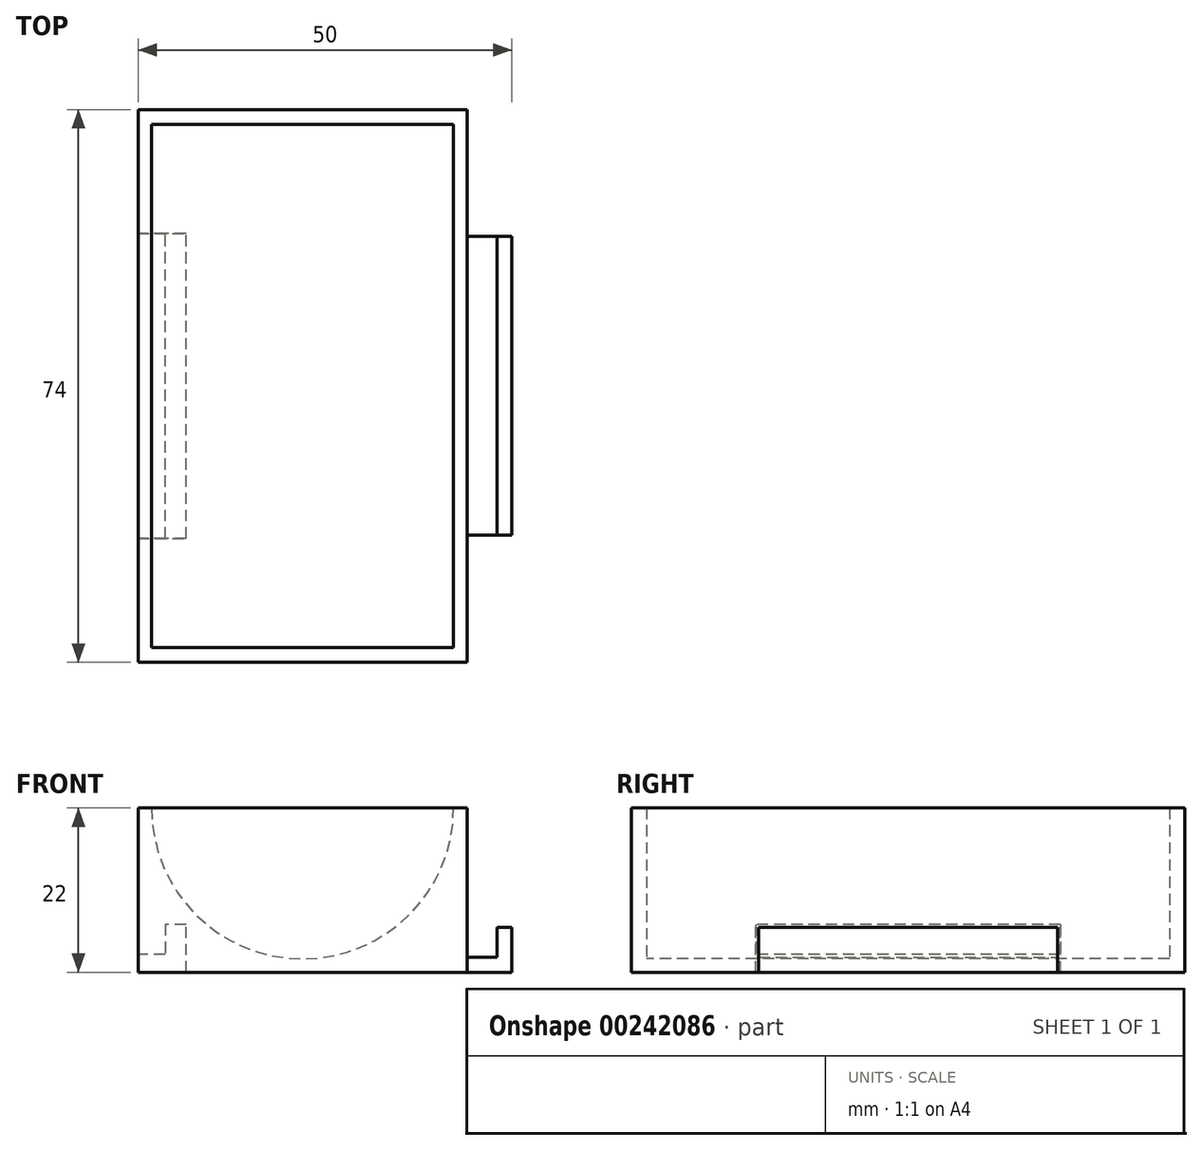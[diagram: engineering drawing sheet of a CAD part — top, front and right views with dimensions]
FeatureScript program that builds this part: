
annotation { "Feature Type Name" : "Feature", "Feature Type Description" : "" }
export const myFeature = defineFeature(function(context is Context, id is Id, definition is map)
    precondition{}
    {
        {
            var Q0;
            Q0=qCreatedBy(makeId("Top.planeOp"),FACE);
            var sketch = newSketch(context, id + "F0", { "sketchPlane" : qUnion([Q0])});
            skLineSegment(sketch, "E0.bottom", {"start": v(0, 0) * mm, "end": v(44, 0) * mm});
            skLineSegment(sketch, "E0.top", {"start": v(0, 70) * mm, "end": v(44, 70) * mm});
            skLineSegment(sketch, "E0.left", {"start": v(0, 0) * mm, "end": v(0, 70) * mm});
            skLineSegment(sketch, "E0.right", {"start": v(44, 0) * mm, "end": v(44, 70) * mm});
            skSolve(sketch);
        }
        {
            var Q0;
            Q0 = qSketchRegion(id + "F0", true);
            var Q1;
            Q1=makeQuery(id+"F0.imprint","IMPRINT",FACE,{"disambiguationData":[TD([[makeQuery(id+"F0.imprint","IMPRINT",EDGE,{"derivedFrom":sQuery(id+"F0.wireOp",EDGE,"E0.bottom")}),1.0]])]});
            extrude(context, id + "F1", {"entities" : qUnion([Q0, Q1]), "depth" : 22 * mm});
        }
        {
            var Q0;
            Q0=makeQuery(id+"F1.opExtrude","SWEPT_FACE",FACE,{"disambiguationData":[OSD([sQuery(id+"F0.wireOp",EDGE,"E0.bottom")])]});
            var sketch = newSketch(context, id + "F2", { "sketchPlane" : qUnion([Q0])});
            skCircle(sketch, "E1", {"center": v(22, 22) * mm, "radius": 20.2 * mm});
            skLineSegment(sketch, "E2.0.0", {"start": v(44, 0) * mm, "end": v(0, 0) * mm});
            skLineSegment(sketch, "E2.0.1", {"start": v(0, 0) * mm, "end": v(0, 22) * mm});
            skLineSegment(sketch, "E2.0.2", {"start": v(0, 22) * mm, "end": v(44, 22) * mm});
            skLineSegment(sketch, "E2.0.3", {"start": v(44, 22) * mm, "end": v(44, 0) * mm});
            skSolve(sketch);
        }
        {
            var Q0;
            {var subQ0=sQuery(id+"F2.wireOp",EDGE,"E2.0.2");var subQ1=sQuery(id+"F2.wireOp",EDGE,"E1");var subQ2=makeQuery(id+"F2.imprint","INTERSECT",VERTEX,{"disambiguationData":[OD(0.0)],"derivedFrom":[subQ1,subQ0]});Q0=makeQuery(id+"F2.imprint","IMPRINT",FACE,{"disambiguationData":[TD([[makeQuery(id+"F2.imprint","IMPRINT",EDGE,{"disambiguationData":[TD([[subQ2,-1.0]])],"derivedFrom":subQ1}),1.0]])]});}
            extrude(context, id + "F3", {"entities" : qUnion([Q0]), "operationType" : NewBodyOperationType.REMOVE, "oppositeDirection" : true, "depth" : 70 * mm});
        }
        {
            var Q0;
            {var subQ0=sQuery(id+"F2.wireOp",EDGE,"E2.0.2");var subQ1=sQuery(id+"F2.wireOp",EDGE,"E1");var subQ2=makeQuery(id+"F2.imprint","INTERSECT",VERTEX,{"disambiguationData":[OD(0.0)],"derivedFrom":[subQ1,subQ0]});Q0=makeQuery(id+"F2.imprint","IMPRINT",FACE,{"disambiguationData":[TD([[makeQuery(id+"F2.imprint","IMPRINT",EDGE,{"disambiguationData":[TD([[subQ2,-1.0]])],"derivedFrom":subQ1}),1.0]])]});}
            var Q1;
            Q1=makeQuery(id+"F2.imprint","IMPRINT",FACE,{"disambiguationData":[TD([[makeQuery(id+"F2.imprint","IMPRINT",EDGE,{"derivedFrom":sQuery(id+"F2.wireOp",EDGE,"E2.0.0")}),1.0]])]});
            extrude(context, id + "F4", {"entities" : qUnion([Q0, Q1]), "operationType" : NewBodyOperationType.ADD, "depth" : 2 * mm});
        }
        {
            var Q0;
            Q0=makeQuery(id+"F1.opExtrude","SWEPT_FACE",FACE,{"disambiguationData":[OSD([sQuery(id+"F0.wireOp",EDGE,"E0.top")])]});
            var sketch = newSketch(context, id + "F5", { "sketchPlane" : qUnion([Q0])});
            skLineSegment(sketch, "E3.0.0", {"start": v(-42.2, 22) * mm, "end": v(-1.8, 22) * mm});
            skArc(sketch, "E3.0.1", {"start": v(-1.8, 22) * mm, "mid": v(-22, 1.8) * mm, "end": v(-42.2, 22) * mm});
            skSolve(sketch);
        }
        {
            var Q0;
            Q0=makeQuery(id+"F5.imprint","IMPRINT",FACE,{"disambiguationData":[TD([[makeQuery(id+"F5.imprint","IMPRINT",EDGE,{"derivedFrom":sQuery(id+"F5.wireOp",EDGE,"E3.0.1")}),1.0]])]});
            var Q1;
            Q1=makeQuery(id+"F5.imprint","IMPRINT",FACE,{"disambiguationData":[TD([[makeQuery(id+"F5.imprint","IMPRINT",EDGE,{"derivedFrom":sQuery(id+"F5.wireOp",EDGE,"E3.0.0")}),-1.0]])]});
            extrude(context, id + "F6", {"entities" : qUnion([Q0, Q1]), "operationType" : NewBodyOperationType.ADD, "depth" : 2 * mm});
        }
        {
            var Q0;
            {var subQ0=sQuery(id+"F0.wireOp",EDGE,"E0.right");Q0=makeQuery(id+"F6.boolean.opBoolean","MERGE",FACE,{"derivedFrom":[makeQuery(id+"F4.boolean.opBoolean","MERGE",FACE,{"derivedFrom":[makeQuery(id+"F1.opExtrude","SWEPT_FACE",FACE,{"disambiguationData":[OSD([subQ0])]}),makeQuery(id+"F4.opExtrude","SWEPT_FACE",FACE,{"disambiguationData":[OSD([sQuery(id+"F2.wireOp",EDGE,"E2.0.3")])]})]}),makeQuery(id+"F6.opExtrude","SWEPT_FACE",FACE,{"disambiguationData":[OSD([sQuery(id+"F0.wireOp",EDGE,"E0.top"),subQ0])]})]});}
            var sketch = newSketch(context, id + "F7", { "sketchPlane" : qUnion([Q0])});
            skLineSegment(sketch, "E4.bottom", {"start": v(35, 0) * mm, "end": v(55, 0) * mm});
            skLineSegment(sketch, "E4.top", {"start": v(35, 2) * mm, "end": v(55, 2) * mm});
            skLineSegment(sketch, "E4.left", {"start": v(35, 0) * mm, "end": v(35, 2) * mm});
            skLineSegment(sketch, "E4.right", {"start": v(55, 0) * mm, "end": v(55, 2) * mm});
            skLineSegment(sketch, "E5.bottom", {"start": v(35, 0) * mm, "end": v(15, 0) * mm});
            skLineSegment(sketch, "E5.top", {"start": v(35, 2) * mm, "end": v(15, 2) * mm});
            skLineSegment(sketch, "E5.right", {"start": v(15, 0) * mm, "end": v(15, 2) * mm});
            skSolve(sketch);
        }
        {
            var Q0;
            Q0=makeQuery(id+"F7.imprint","IMPRINT",FACE,{"disambiguationData":[TD([[makeQuery(id+"F7.imprint","IMPRINT",EDGE,{"derivedFrom":sQuery(id+"F7.wireOp",EDGE,"E5.bottom")}),1.0]])]});
            var Q1;
            Q1=makeQuery(id+"F7.imprint","IMPRINT",FACE,{"disambiguationData":[TD([[makeQuery(id+"F7.imprint","IMPRINT",EDGE,{"derivedFrom":sQuery(id+"F7.wireOp",EDGE,"E4.bottom")}),1.0]])]});
            extrude(context, id + "F8", {"entities" : qUnion([Q0, Q1]), "depth" : 6 * mm});
        }
        {
            var Q0;
            Q0=makeQuery(id+"F8.opExtrude","SWEPT_FACE",FACE,{"disambiguationData":[OSD([sQuery(id+"F7.wireOp",EDGE,"E4.top"),sQuery(id+"F7.wireOp",EDGE,"E5.top")])]});
            var sketch = newSketch(context, id + "F9", { "sketchPlane" : qUnion([Q0])});
            skLineSegment(sketch, "E6.bottom", {"start": v(50, 15) * mm, "end": v(48, 15) * mm});
            skLineSegment(sketch, "E6.top", {"start": v(50, 55) * mm, "end": v(48, 55) * mm});
            skLineSegment(sketch, "E6.left", {"start": v(50, 15) * mm, "end": v(50, 55) * mm});
            skLineSegment(sketch, "E6.right", {"start": v(48, 15) * mm, "end": v(48, 55) * mm});
            skSolve(sketch);
        }
        {
            var Q0;
            Q0=makeQuery(id+"F9.imprint","IMPRINT",FACE,{"disambiguationData":[TD([[makeQuery(id+"F9.imprint","IMPRINT",EDGE,{"derivedFrom":sQuery(id+"F9.wireOp",EDGE,"E6.bottom")}),-1.0]])]});
            extrude(context, id + "F10", {"entities" : qUnion([Q0]), "operationType" : NewBodyOperationType.ADD, "depth" : 4 * mm});
        }
        {
            var Q0;
            Q0=makeQuery(id+"F8.opExtrude","SWEPT_BODY",BODY,{"disambiguationData":[OSD([sQuery(id+"F7.wireOp",EDGE,"E4.bottom"),sQuery(id+"F7.wireOp",EDGE,"E4.top"),sQuery(id+"F7.wireOp",EDGE,"E4.right"),sQuery(id+"F7.wireOp",EDGE,"E5.bottom"),sQuery(id+"F7.wireOp",EDGE,"E5.top"),sQuery(id+"F7.wireOp",EDGE,"E5.right")])]});
            var Q1;
            Q1=makeQuery(id+"F4.opExtrude","CAP_EDGE",EDGE,{"disambiguationData":[OSD([sQuery(id+"F2.wireOp",EDGE,"E2.0.0")])],"isStart":false});
            var Q2;
            Q2=makeQuery(id+"F4.opExtrude","CAP_EDGE",EDGE,{"disambiguationData":[OSD([sQuery(id+"F2.wireOp",EDGE,"E2.0.0")])],"isStart":false});
            transform(context, id + "F11", {"entities" : qUnion([Q0]), "transformType" : TransformType.TRANSLATION_DISTANCE, "transformDirection" : qUnion([Q2]), "distance" : 44 * mm, "oppositeDirection" : true, "makeCopy" : true});
        }
        {
            var Q0;
            Q0=makeQuery(id+"F11.opPattern","COPY",BODY,{"derivedFrom":makeQuery(id+"F8.opExtrude","SWEPT_BODY",BODY,{"disambiguationData":[OSD([sQuery(id+"F7.wireOp",EDGE,"E4.bottom"),sQuery(id+"F7.wireOp",EDGE,"E4.top"),sQuery(id+"F7.wireOp",EDGE,"E4.right"),sQuery(id+"F7.wireOp",EDGE,"E5.bottom"),sQuery(id+"F7.wireOp",EDGE,"E5.top"),sQuery(id+"F7.wireOp",EDGE,"E5.right")])]}),"instanceName":"1"});
            var Q1;
            Q1=makeQuery(id+"F1.opExtrude","SWEPT_BODY",BODY,{"disambiguationData":[OSD([sQuery(id+"F0.wireOp",EDGE,"E0.bottom"),sQuery(id+"F0.wireOp",EDGE,"E0.top"),sQuery(id+"F0.wireOp",EDGE,"E0.left"),sQuery(id+"F0.wireOp",EDGE,"E0.right")])]});
            var Q2;
            Q2=makeQuery(id+"F11.opPattern","COPY",FACE,{"derivedFrom":makeQuery(id+"F8.opExtrude","CAP_FACE",FACE,{"disambiguationData":[OSD([sQuery(id+"F7.wireOp",EDGE,"E4.bottom"),sQuery(id+"F7.wireOp",EDGE,"E4.top"),sQuery(id+"F7.wireOp",EDGE,"E4.right"),sQuery(id+"F7.wireOp",EDGE,"E5.bottom"),sQuery(id+"F7.wireOp",EDGE,"E5.top"),sQuery(id+"F7.wireOp",EDGE,"E5.right")])],"isStart":true}),"instanceName":"1"});
            var Q3;
            Q3=makeQuery(id+"F11.opPattern","COPY",FACE,{"derivedFrom":makeQuery(id+"F8.opExtrude","SWEPT_FACE",FACE,{"disambiguationData":[OSD([sQuery(id+"F7.wireOp",EDGE,"E4.bottom"),sQuery(id+"F7.wireOp",EDGE,"E5.bottom")])]}),"instanceName":"1"});
            booleanBodies(context, id + "F12", {"operationType" : BooleanOperationType.SUBTRACTION, "tools" : qUnion([Q0]), "targets" : qUnion([Q1]), "offset" : true, "offsetAll" : true, "entitiesToOffset" : qUnion([Q2, Q3]), "offsetDistance" : 0.4 * mm});
        }
    });
